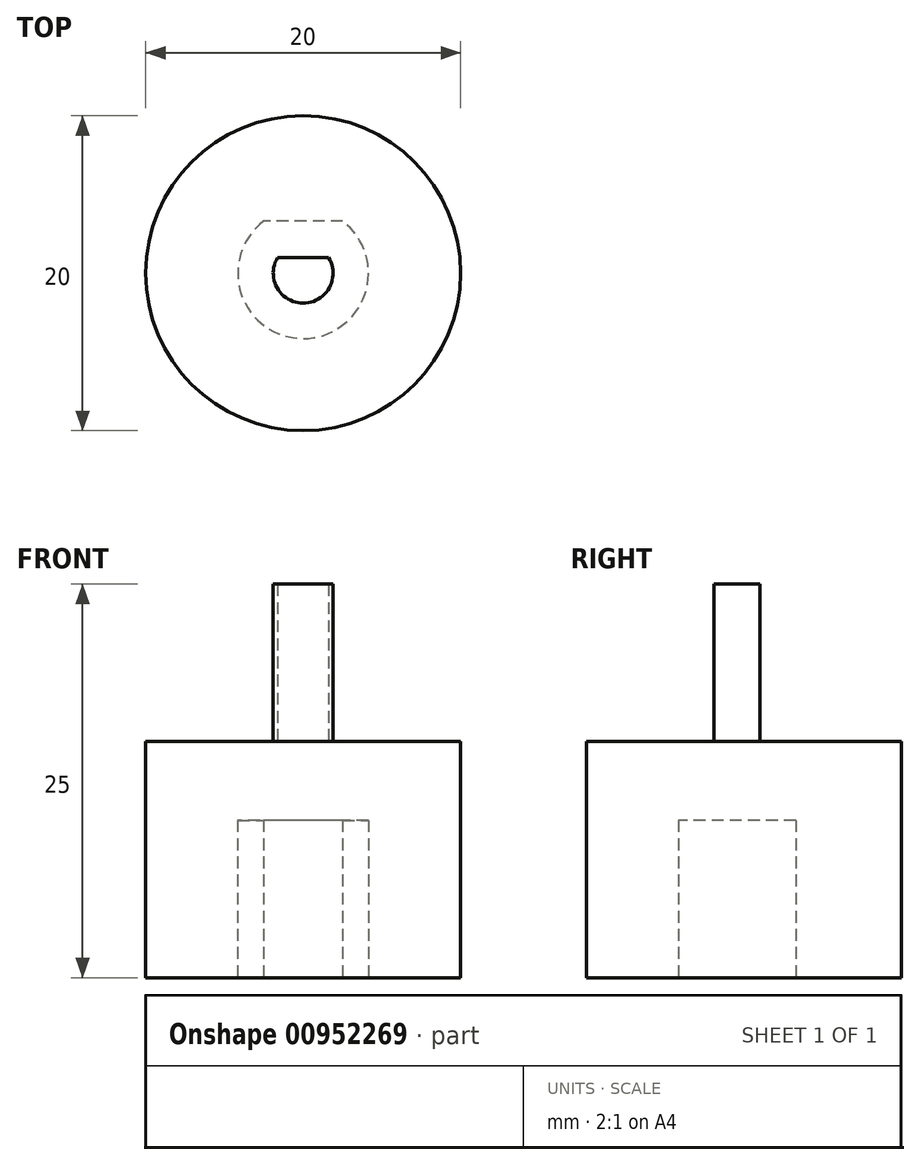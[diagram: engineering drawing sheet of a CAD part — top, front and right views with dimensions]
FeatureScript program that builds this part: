
annotation { "Feature Type Name" : "Feature", "Feature Type Description" : "" }
export const myFeature = defineFeature(function(context is Context, id is Id, definition is map)
    precondition{}
    {
        {
            var Q0;
            Q0=qCreatedBy(makeId("Top.planeOp"),FACE);
            var sketch = newSketch(context, id + "F0", { "sketchPlane" : qUnion([Q0])});
            skCircle(sketch, "E0", {"center": v(0, 0) * mm, "radius": 10 * mm});
            skSolve(sketch);
        }
        {
            var Q0;
            Q0 = qSketchRegion(id + "F0", true);
            extrude(context, id + "F1", {"entities" : qUnion([Q0]), "depth" : 15 * mm, "offsetDistance" : 25 * mm});
        }
        {
            var Q0;
            Q0=makeQuery(id+"F1.opExtrude","CAP_FACE",FACE,{"disambiguationData":[OSD([sQuery(id+"F0.wireOp",EDGE,"E0")])],"isStart":true});
            var sketch = newSketch(context, id + "F2", { "sketchPlane" : qUnion([Q0])});
            skArc(sketch, "E1", {"start": v(2.52, -3.3) * mm, "mid": v(0, 4.15) * mm, "end": v(-2.52, -3.3) * mm});
            skLineSegment(sketch, "E2", {"start": v(2.52, -3.3) * mm, "end": v(-2.52, -3.3) * mm});
            skSolve(sketch);
        }
        {
            var Q0;
            Q0 = qSketchRegion(id + "F2", true);
            extrude(context, id + "F3", {"entities" : qUnion([Q0]), "operationType" : NewBodyOperationType.REMOVE, "oppositeDirection" : true, "depth" : 10 * mm, "offsetDistance" : 25 * mm});
        }
        {
            var Q0;
            Q0=makeQuery(id+"F1.opExtrude","CAP_FACE",FACE,{"disambiguationData":[OSD([sQuery(id+"F0.wireOp",EDGE,"E0")])],"isStart":false});
            var sketch = newSketch(context, id + "F4", { "sketchPlane" : qUnion([Q0])});
            skArc(sketch, "E3.converted", {"start": v(-1.62, 1) * mm, "mid": v(0, -1.9) * mm, "end": v(1.62, 1) * mm});
            skLineSegment(sketch, "E4", {"start": v(-1.62, 1) * mm, "end": v(1.62, 1) * mm});
            skSolve(sketch);
        }
        {
            var Q0;
            Q0 = qSketchRegion(id + "F4", true);
            extrude(context, id + "F5", {"entities" : qUnion([Q0]), "operationType" : NewBodyOperationType.ADD, "depth" : 10 * mm, "offsetDistance" : 25 * mm});
        }
    });
